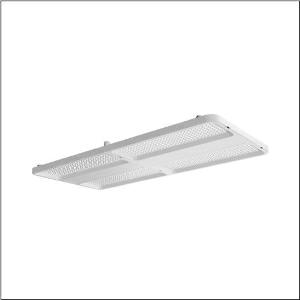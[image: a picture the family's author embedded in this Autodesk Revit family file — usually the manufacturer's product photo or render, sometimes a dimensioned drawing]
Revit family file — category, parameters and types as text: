
# Revit family: highbay_21_maxi_52hn12db4mba
name_source: partatom
category: Lighting Fixtures
units: mm (PartAtom-declared; Revit-internal decimal feet)

## family parameters
Cut with Voids When Loaded = No
Host = Face
Light Source = No
Part Type = Normal
Room Calculation Point = No
Round Connector Dimension = Use Diameter
Shared = No

## types (1)
- --- (1 x LED, 4230 lm, 22.6 W, 4000K)
    Apparent Load = 23 VA
    CIE Flux Codes = 90 98 100 100 100
    Color Rendering = 80
    Color Temperature = 4000K
    Default Elevation = 1800 mm
    Description = high bay luminaire Highbay 21 maxi; direct symmetric wide distribution, light control with lens of PMMA; UGR ≤ 22 (X = 4H | Y = 8H | S = 0.25H | reflection values 70/50/20); luminous flux: 28.000lm; light colour: 840, colour temperature: 4000K, MacAdam ≤ 3 SDCM (initial), colour rendering: CRI > 80; luminous efficacy: 194,4lm/W; rated service life: 75.000h (L80) at AT= ta max; control: DALI 2; luminaire connection: terminal, 5-pole, max. 2.5mm² (cable entry for one cable, Ø 8.5..16mm); mains connection: 230..240V, AC/DC 0/50..60Hz; connected load: 144W; protection rating (complete): IP40; insulation class (complete): insulation class I (protective earthing); protection symbol: D; impact resistance: IK08; certification: CE, ENEC, VDE, UKCA; luminaire for central battery installations according to EN 60598-2-22, internal wiring halogen-free; luminaire LABS conformity tested according to VDMA 24364:2018-05; ball impact resistant only with use of appropriate mounting accessories; Suitable for use in the food industry according to the specifications of IFS-Food, HACCP and/or BRC; housing frame of high-performance plastic PA6, matt traffic white (RAL 9016); cover of PMMA; dimension (LxWxH): 946 x 442 x 72mm; permissible operating ambient temperature: -40..+65°C (reducing of maximum allowable ambient temperature of 5°C with ceiling mounting); packaging unit: 1 piece; (delivery without accessories; please order mounting accessories separately)
    Height = 72 mm  [stored 0.23622 ft]
    Lamp = 1 x LED
    Lamp Light Flux = 4230 lm
    Lamp Power = 22.6 W
    Lamp count = 1
    Length = 946 mm
    Luminous efficacy = 187 lm/W
    Manufacturer = Siteco
    ModVariant = No
    Model = 52HN12DB4MBA
    Mounting Place = Ceiling
    Mounting Type = Pendant
    Number of Poles = 1
    OnlyDefault = Yes
    Power Factor = 1
    Product Name = Highbay 21 maxi
    Product group = high bay luminaire
    ProductGroupID = 902
    Protection Class = Protection class I
    Protection Degree = IP 40
    RLX_Detail_Level = 1
    RLX_Emergency_Light_Flux = 0 lm
    RLX_Emergency_Type = 0
    RLX_Emergency_Type_DB = No
    RlxData = <blob elided: 128525 chars, md5=afa19f27>
    Socket = socket
    Standby Power = 0 W
    System Light Flux = 4230 lm
    System Power = 23 W
    Type Comments = : DC mode (central or group accumulator) initial emergency light level
    Type Image = l_1376023.jpg
    URL = http://relux.com
    VarID = @adj_012491
    Voltage = 0 V
    Weight = 0.00 kg
    Width = 442 mm

note: [stored X ft] marks values corroborated as IEEE doubles in the binary element streams (Revit-internal decimal feet)

## geometry (parser evidence)
native form markers: Blend x4, Sweep x10
no freeform markers — native parametric forms only
